# Revit family: KS Polar plus, DS 20, Ø 10- 88,9
name_source: partatom
category: HLS-Bauteile
revit_build: Autodesk Revit 2018 (Build: 20190510_1515(x64)
units: mm (PartAtom-declared; Revit-internal decimal feet)

## family parameters
Arbeitsebenenbasiert = Ja
Beim Laden mit Abzugskörper schneiden = Nein
Bemaßung runder Anschluss = Durchmesser verwenden
Gemeinsam genutzt = Ja
Immer vertikal = Nein
Raumberechnungspunkt = Nein
Teiletyp = Normal

## types (23) — shared parameters
Anschluss = M8/M10
BP = 14 mm  [stored 0.0459318 ft]
Baustoffklasse = B2
DS = 20 mm  [stored 0.0656168 ft]
DVS = 5 mm  [stored 0.0164042 ft]
Dichte Kern = 145 kg/m³
Dämmkörper = AC/PU
Dämmstärke = 20 mm  [stored 0.0656168 ft]
Fabrikat = MEFA
Firma = MEFA Befestigungs- und Montagesysteme GmbH
HGA = 17 mm  [stored 0.0557743 ft]
Kurztext1 = Kälteschelle Polar Plus
Material = Stahl
Materialname = DD11
Mengeneinheit = St
Oberflaeche = galvanisch verzinkt
Rohrschellentyp = Omnia MB
Vorgabe-Ansicht = 1219 mm
Wasserdampfdiffusionswiderstand = 7000 µ
Wärmeleitfähigkeit = 0.031 W/mK
d1 = 7 mm  [stored 0.0229659 ft]
max. Temperaturbeständigkeit = 105 °C
mittl. Nenndruckfestigkeit Kern = 1,9 N/mm²
stat. Belastung Kern = 0,38 N/mm²

## per-type parameters (varying)
- Kälteschelle Polar plus, DS 20, M8/M10, Ø 10: A=39 mm; AB=0 mm  [stored 0 ft]; Anschlußhöhe=37 mm; Artikelnummer=74620100; B=89 mm; Breite=89 mm; D=10 mm  [stored 0.0328084 ft]; D0=50 mm; DF1=16 mm  [stored 0.0524934 ft]; DF2=14 mm  [stored 0.0459318 ft]; Dmax=15 mm  [stored 0.0492126 ft]; Dmin=10 mm  [stored 0.0328084 ft]; EAN=4250928448651; Gewicht=0.11 kg; Gewicht pro Bauteil=0.11 kg; H=71 mm; Kurztext2=10 mm Iso 20 x 36 mm M8/M10; L=36 mm  [stored 0.11811 ft]; MB=20 mm  [stored 0.0656168 ft]; MD=2 mm  [stored 0.00656168 ft]; R=25 mm  [stored 0.082021 ft]; RM=27 mm; Rohraußendurchmesser Kupfer=10 mm; S=73 mm; Schalenlänge=36 mm; max. zul. Last=0.18 kN; vpe=20 St
- Kälteschelle Polar plus, DS 20, M8/M10, Ø 17,2: A=39 mm; AB=1 mm  [stored 0.00328084 ft]; Anschlußhöhe=38 mm; Artikelnummer=74620170; B=92 mm; Breite=92 mm; D=17 mm  [stored 0.0557743 ft]; D0=57 mm; DF1=15 mm  [stored 0.0492126 ft]; DF2=15 mm  [stored 0.0492126 ft]; Dmax=18 mm  [stored 0.0590551 ft]; Dmin=16 mm  [stored 0.0524934 ft]; EAN=4250928442451; Gewicht=0.12 kg; Gewicht pro Bauteil=0.12 kg; H=78 mm; Kurztext2=17,2 mm Iso 20 x 36 mm M8/M10; L=36 mm  [stored 0.11811 ft]; MB=20 mm  [stored 0.0656168 ft]; MD=2 mm  [stored 0.00656168 ft]; R=29 mm; RM=31 mm; Rohraußendurchmesser Stahl=17,2 mm; S=77 mm; Schalenlänge=36 mm; max. zul. Last=0.21 kN; vpe=20 St
- Kälteschelle Polar plus, DS 20, M8/M10, Ø 26,9: A=39 mm; AB=0 mm  [stored 0 ft]; Anschlußhöhe=37 mm; Artikelnummer=74620270; B=101 mm; Breite=101 mm; D=27 mm; D0=67 mm; DF1=14 mm  [stored 0.0459318 ft]; DF2=15 mm  [stored 0.0492126 ft]; Dmax=28 mm; Dmin=27 mm; EAN=4250928442499; Gewicht=0.13 kg; Gewicht pro Bauteil=0.13 kg; H=88 mm; Kurztext2=26,9 mm Iso 20 x 36 mm M8/M10; L=36 mm  [stored 0.11811 ft]; MB=20 mm  [stored 0.0656168 ft]; MD=2 mm  [stored 0.00656168 ft]; R=33 mm; RM=35 mm  [stored 0.114829 ft]; Rohraußendurchmesser Stahl=26,9 mm; S=87 mm; Schalenlänge=36 mm; max. zul. Last=0.32 kN; vpe=20 St
- Kälteschelle Polar plus, DS 20, M8/M10, Ø 32: A=39 mm; AB=0 mm  [stored 0 ft]; Anschlußhöhe=40 mm; Artikelnummer=74620320; B=113 mm; Breite=113 mm; D=32 mm; D0=72 mm; DF1=16 mm  [stored 0.0524934 ft]; DF2=16 mm  [stored 0.0524934 ft]; Dmax=37 mm; Dmin=32 mm; EAN=4250928442512; Gewicht=0.14 kg; Gewicht pro Bauteil=0.14 kg; H=93 mm; Kurztext2=32 mm Iso 20 x 36 mm M8/M10; L=36 mm  [stored 0.11811 ft]; MB=20 mm  [stored 0.0656168 ft]; MD=2 mm  [stored 0.00656168 ft]; R=36 mm  [stored 0.11811 ft]; RM=38 mm  [stored 0.124672 ft]; Rohraußendurchmesser Kunststoff=32 mm; S=97 mm; Schalenlänge=36 mm; max. zul. Last=0.38 kN; vpe=20 St
- Kälteschelle Polar plus, DS 20, M8/M10, Ø 40: A=39 mm; AB=0 mm  [stored 0 ft]; Anschlußhöhe=40 mm; Artikelnummer=74620400; B=117 mm; Breite=117 mm; D=40 mm; D0=80 mm; DF1=15 mm  [stored 0.0492126 ft]; DF2=15 mm  [stored 0.0492126 ft]; Dmax=43 mm; Dmin=40 mm; EAN=4250928442543; Gewicht=0.15 kg; Gewicht pro Bauteil=0.15 kg; H=101 mm; Kurztext2=40 mm Iso 20 x 36 mm M8/M10; L=36 mm  [stored 0.11811 ft]; MB=20 mm  [stored 0.0656168 ft]; MD=2 mm  [stored 0.00656168 ft]; R=40 mm; RM=42 mm; Rohraußendurchmesser Kunststoff=40 mm; S=102 mm; Schalenlänge=36 mm; max. zul. Last=0.48 kN; vpe=20 St
- Kälteschelle Polar plus, DS 20, M8/M10, Ø 48,3: A=39 mm; AB=0 mm  [stored 0 ft]; Anschlußhöhe=39 mm; Artikelnummer=74620480; B=124 mm; Breite=124 mm; D=48 mm; D0=88 mm; DF1=13 mm; DF2=13 mm; Dmax=54 mm; Dmin=48 mm; EAN=4250928442567; Gewicht=0.16 kg; Gewicht pro Bauteil=0.16 kg; H=109 mm; Kurztext2=48,3 mm Iso 20 x 36 mm M8/M10; L=36 mm  [stored 0.11811 ft]; MB=20 mm  [stored 0.0656168 ft]; MD=2 mm  [stored 0.00656168 ft]; R=44 mm; RM=46 mm  [stored 0.150919 ft]; Rohraußendurchmesser Stahl=48,3 mm; S=111 mm; Schalenlänge=36 mm; max. zul. Last=0.58 kN; vpe=20 St
- Kälteschelle Polar plus, DS 20, M8/M10, Ø 57: A=40 mm; AB=0 mm  [stored 0 ft]; Anschlußhöhe=40 mm; Artikelnummer=74620570; B=136 mm; Breite=136 mm; D=57 mm; D0=97 mm; DF1=15 mm  [stored 0.0492126 ft]; DF2=15 mm  [stored 0.0492126 ft]; Dmax=61 mm; Dmin=57 mm; EAN=4250928442598; Gewicht=0.24 kg; Gewicht pro Bauteil=0.24 kg; H=119 mm; Kurztext2=57 mm Iso 20 x 41 mm M8/M10; L=41 mm; MB=25 mm  [stored 0.082021 ft]; MD=3 mm  [stored 0.00984252 ft]; R=49 mm; RM=51 mm; Rohraußendurchmesser Stahl=57 mm; S=121 mm; Schalenlänge=41 mm; max. zul. Last=0.79 kN; vpe=20 St
- Kälteschelle Polar plus, DS 20, M8/M10, Ø 63,5: A=40 mm; AB=2 mm  [stored 0.00656168 ft]; Anschlußhöhe=39 mm; Artikelnummer=74620640; B=143 mm; Breite=143 mm; D=64 mm; D0=104 mm; DF1=16 mm  [stored 0.0524934 ft]; DF2=16 mm  [stored 0.0524934 ft]; Dmax=66 mm; Dmin=62 mm; EAN=4250928442611; Gewicht=0.25 kg; Gewicht pro Bauteil=0.25 kg; H=126 mm; Kurztext2=63,5 mm Iso 20 x 41 mm M8/M10; L=41 mm; MB=25 mm  [stored 0.082021 ft]; MD=3 mm  [stored 0.00984252 ft]; R=52 mm; RM=55 mm; Rohraußendurchmesser Kupfer=64 mm; Rohraußendurchmesser Stahl=63,5 mm; S=127 mm; Schalenlänge=41 mm; max. zul. Last=0.89 kN; vpe=15 St
- Kälteschelle Polar plus, DS 20, M8/M10, Ø 75: A=40 mm; AB=0 mm  [stored 0 ft]; Anschlußhöhe=39 mm; Artikelnummer=74620750; B=158 mm; Breite=152 mm; D=75 mm; D0=115 mm; DF1=17 mm  [stored 0.0557743 ft]; DF2=16 mm  [stored 0.0524934 ft]; Dmax=80 mm; Dmin=75 mm; EAN=4250928442628; Gewicht=0.28 kg; Gewicht pro Bauteil=0.28 kg; H=137 mm; Kurztext2=75 mm Iso 20 x 41 mm M8/M10; L=41 mm; MB=25 mm  [stored 0.082021 ft]; MD=3 mm  [stored 0.00984252 ft]; R=58 mm; RM=60 mm; Rohraußendurchmesser Kunststoff=75 mm; S=141 mm; Schalenlänge=41 mm; max. zul. Last=1.05 kN; vpe=15 St
- Kälteschelle Polar plus, DS 20, M8/M10, Ø 88,9: A=40 mm; AB=1 mm  [stored 0.00328084 ft]; Anschlußhöhe=39 mm; Artikelnummer=74620890; B=165 mm; Breite=165 mm; D=89 mm; D0=129 mm; DF1=15 mm  [stored 0.0492126 ft]; DF2=15 mm  [stored 0.0492126 ft]; Dmax=90 mm; Dmin=88 mm; EAN=4250928442642; Gewicht=0.30 kg; Gewicht pro Bauteil=0.30 kg; H=151 mm; Kurztext2=88,9 mm Iso 20 x 41 mm M8/M10; L=41 mm; MB=25 mm  [stored 0.082021 ft]; MD=3 mm  [stored 0.00984252 ft]; R=64 mm; RM=67 mm; Rohraußendurchmesser Stahl=88,9 mm; S=150 mm; Schalenlänge=41 mm; max. zul. Last=1.24 kN; vpe=15 St
- Kälteschelle Polar plus, DS 20, M8/M10, Ø 12: A=39 mm; AB=2 mm  [stored 0.00656168 ft]; Anschlußhöhe=37 mm; Artikelnummer=74620120; B=89 mm; Breite=89 mm; D=12 mm  [stored 0.0393701 ft]; D0=52 mm; DF1=16 mm  [stored 0.0524934 ft]; DF2=14 mm  [stored 0.0459318 ft]; Dmax=15 mm  [stored 0.0492126 ft]; Dmin=10 mm  [stored 0.0328084 ft]; EAN=4250928448668; Gewicht=0.11 kg; Gewicht pro Bauteil=0.11 kg; H=73 mm; Kurztext2=12 mm Iso 20 x 36 mm M8/M10; L=36 mm  [stored 0.11811 ft]; MB=20 mm  [stored 0.0656168 ft]; MD=2 mm  [stored 0.00656168 ft]; R=26 mm; RM=28 mm; Rohraußendurchmesser Kupfer=12 mm; S=73 mm; Schalenlänge=36 mm; max. zul. Last=0.18 kN; vpe=20 St
- Kälteschelle Polar plus, DS 20, M8/M10, Ø 15: A=39 mm; AB=5 mm  [stored 0.0164042 ft]; Anschlußhöhe=37 mm; Artikelnummer=74620150; B=89 mm; Breite=89 mm; D=15 mm  [stored 0.0492126 ft]; D0=55 mm; DF1=16 mm  [stored 0.0524934 ft]; DF2=14 mm  [stored 0.0459318 ft]; Dmax=15 mm  [stored 0.0492126 ft]; Dmin=10 mm  [stored 0.0328084 ft]; EAN=4250928442444; Gewicht=0.11 kg; Gewicht pro Bauteil=0.11 kg; H=76 mm; Kurztext2=15 mm Iso 20 x 36 mm M8/M10; L=36 mm  [stored 0.11811 ft]; MB=20 mm  [stored 0.0656168 ft]; MD=2 mm  [stored 0.00656168 ft]; R=28 mm; RM=30 mm  [stored 0.0984252 ft]; Rohraußendurchmesser Kupfer=15 mm; S=73 mm; Schalenlänge=36 mm; max. zul. Last=0.18 kN; vpe=20 St
- Kälteschelle Polar plus, DS 20, M8/M10, Ø 18: A=39 mm; AB=2 mm  [stored 0.00656168 ft]; Anschlußhöhe=38 mm; Artikelnummer=74620180; B=92 mm; Breite=92 mm; D=18 mm  [stored 0.0590551 ft]; D0=58 mm; DF1=15 mm  [stored 0.0492126 ft]; DF2=15 mm  [stored 0.0492126 ft]; Dmax=18 mm  [stored 0.0590551 ft]; Dmin=16 mm  [stored 0.0524934 ft]; EAN=4250928442468; Gewicht=0.12 kg; Gewicht pro Bauteil=0.12 kg; H=79 mm; Kurztext2=18 mm Iso 20 x 36 mm M8/M10; L=36 mm  [stored 0.11811 ft]; MB=20 mm  [stored 0.0656168 ft]; MD=2 mm  [stored 0.00656168 ft]; R=29 mm; RM=31 mm; Rohraußendurchmesser Kupfer=18 mm; S=77 mm; Schalenlänge=36 mm; max. zul. Last=0.21 kN; vpe=20 St
- Kälteschelle Polar plus, DS 20, M8/M10, Ø 21,3: A=39 mm; AB=0 mm  [stored 0 ft]; Anschlußhöhe=37 mm; Artikelnummer=74620210; B=92 mm; Breite=92 mm; D=21 mm  [stored 0.0688976 ft]; D0=61 mm; DF1=13 mm; DF2=13 mm; Dmax=22 mm  [stored 0.0721785 ft]; Dmin=21 mm  [stored 0.0688976 ft]; EAN=4250928442475; Gewicht=0.12 kg; Gewicht pro Bauteil=0.12 kg; H=82 mm; Kurztext2=21,3 mm Iso 20 x 36 mm M8/M10; L=36 mm  [stored 0.11811 ft]; MB=20 mm  [stored 0.0656168 ft]; MD=2 mm  [stored 0.00656168 ft]; R=31 mm; RM=33 mm; Rohraußendurchmesser Stahl=21,3 mm; S=79 mm; Schalenlänge=36 mm; max. zul. Last=0.25 kN; vpe=20 St
- Kälteschelle Polar plus, DS 20, M8/M10, Ø 22: A=39 mm; AB=1 mm  [stored 0.00328084 ft]; Anschlußhöhe=37 mm; Artikelnummer=74620220; B=92 mm; Breite=92 mm; D=22 mm  [stored 0.0721785 ft]; D0=62 mm; DF1=13 mm; DF2=13 mm; Dmax=22 mm  [stored 0.0721785 ft]; Dmin=21 mm  [stored 0.0688976 ft]; EAN=4250928442482; Gewicht=0.12 kg; Gewicht pro Bauteil=0.12 kg; H=83 mm; Kurztext2=22 mm Iso 20 x 36 mm M8/M10; L=36 mm  [stored 0.11811 ft]; MB=20 mm  [stored 0.0656168 ft]; MD=2 mm  [stored 0.00656168 ft]; R=31 mm; RM=33 mm; Rohraußendurchmesser Kupfer=22 mm; S=79 mm; Schalenlänge=36 mm; max. zul. Last=0.26 kN; vpe=20 St
- Kälteschelle Polar plus, DS 20, M8/M10, Ø 28: A=39 mm; AB=1 mm  [stored 0.00328084 ft]; Anschlußhöhe=37 mm; Artikelnummer=74620280; B=101 mm; Breite=101 mm; D=28 mm; D0=68 mm; DF1=14 mm  [stored 0.0459318 ft]; DF2=15 mm  [stored 0.0492126 ft]; Dmax=28 mm; Dmin=27 mm; EAN=4250928442505; Gewicht=0.13 kg; Gewicht pro Bauteil=0.13 kg; H=89 mm; Kurztext2=28 mm Iso 20 x 36 mm M8/M10; L=36 mm  [stored 0.11811 ft]; MB=20 mm  [stored 0.0656168 ft]; MD=2 mm  [stored 0.00656168 ft]; R=34 mm; RM=36 mm  [stored 0.11811 ft]; Rohraußendurchmesser Kupfer=28 mm; S=87 mm; Schalenlänge=36 mm; max. zul. Last=0.33 kN; vpe=20 St
- Kälteschelle Polar plus, DS 20, M8/M10, Ø 33,7: A=39 mm; AB=2 mm  [stored 0.00656168 ft]; Anschlußhöhe=38 mm; Artikelnummer=74620340; B=113 mm; Breite=113 mm; D=34 mm; D0=74 mm; DF1=16 mm  [stored 0.0524934 ft]; DF2=16 mm  [stored 0.0524934 ft]; Dmax=37 mm; Dmin=32 mm; EAN=4250928442529; Gewicht=0.14 kg; Gewicht pro Bauteil=0.14 kg; H=95 mm; Kurztext2=33,7 mm Iso 20 x 36 mm M8/M10; L=36 mm  [stored 0.11811 ft]; MB=20 mm  [stored 0.0656168 ft]; MD=2 mm  [stored 0.00656168 ft]; R=37 mm; RM=39 mm; Rohraußendurchmesser Stahl=33,7 mm; S=97 mm; Schalenlänge=36 mm; max. zul. Last=0.40 kN; vpe=20 St
- Kälteschelle Polar plus, DS 20, M8/M10, Ø 35: A=39 mm; AB=3 mm  [stored 0.00984252 ft]; Anschlußhöhe=38 mm; Artikelnummer=74620350; B=113 mm; Breite=113 mm; D=35 mm  [stored 0.114829 ft]; D0=75 mm; DF1=16 mm  [stored 0.0524934 ft]; DF2=16 mm  [stored 0.0524934 ft]; Dmax=37 mm; Dmin=32 mm; EAN=4250928442536; Gewicht=0.14 kg; Gewicht pro Bauteil=0.14 kg; H=96 mm; Kurztext2=35 mm Iso 20 x 36 mm M8/M10; L=36 mm  [stored 0.11811 ft]; MB=20 mm  [stored 0.0656168 ft]; MD=2 mm  [stored 0.00656168 ft]; R=38 mm  [stored 0.124672 ft]; RM=40 mm; Rohraußendurchmesser Kupfer=35 mm; S=97 mm; Schalenlänge=36 mm; max. zul. Last=0.42 kN; vpe=20 St
- Kälteschelle Polar plus, DS 20, M8/M10, Ø 42,4: A=39 mm; AB=2 mm  [stored 0.00656168 ft]; Anschlußhöhe=38 mm; Artikelnummer=74620430; B=117 mm; Breite=117 mm; D=42 mm; D0=82 mm; DF1=15 mm  [stored 0.0492126 ft]; DF2=15 mm  [stored 0.0492126 ft]; Dmax=43 mm; Dmin=40 mm; EAN=4250928442550; Gewicht=0.15 kg; Gewicht pro Bauteil=0.15 kg; H=103 mm; Kurztext2=42,4 mm Iso 20 x 36 mm M8/M10; L=36 mm  [stored 0.11811 ft]; MB=20 mm  [stored 0.0656168 ft]; MD=2 mm  [stored 0.00656168 ft]; R=41 mm; RM=43 mm; Rohraußendurchmesser Kupfer=42 mm; Rohraußendurchmesser Stahl=42,4 mm; S=102 mm; Schalenlänge=36 mm; max. zul. Last=0.51 kN; vpe=20 St
- Kälteschelle Polar plus, DS 20, M8/M10, Ø 50: A=39 mm; AB=2 mm  [stored 0.00656168 ft]; Anschlußhöhe=39 mm; Artikelnummer=74620500; B=124 mm; Breite=124 mm; D=50 mm; D0=90 mm; DF1=13 mm; DF2=13 mm; Dmax=54 mm; Dmin=48 mm; EAN=4250928442574; Gewicht=0.16 kg; Gewicht pro Bauteil=0.16 kg; H=111 mm; Kurztext2=50 mm Iso 20 x 36 mm M8/M10; L=36 mm  [stored 0.11811 ft]; MB=20 mm  [stored 0.0656168 ft]; MD=2 mm  [stored 0.00656168 ft]; R=45 mm; RM=47 mm; Rohraußendurchmesser Kunststoff=50 mm; S=111 mm; Schalenlänge=36 mm; max. zul. Last=0.60 kN; vpe=20 St
- Kälteschelle Polar plus, DS 20, M8/M10, Ø 54: A=39 mm; AB=6 mm  [stored 0.019685 ft]; Anschlußhöhe=37 mm; Artikelnummer=74620540; B=124 mm; Breite=124 mm; D=54 mm; D0=94 mm; DF1=13 mm; DF2=13 mm; Dmax=54 mm; Dmin=48 mm; EAN=4250928442581; Gewicht=0.16 kg; Gewicht pro Bauteil=0.16 kg; H=115 mm; Kurztext2=54 mm Iso 20 x 36 mm M8/M10; L=36 mm  [stored 0.11811 ft]; MB=20 mm  [stored 0.0656168 ft]; MD=2 mm  [stored 0.00656168 ft]; R=47 mm; RM=49 mm; Rohraußendurchmesser Kupfer=54 mm; S=111 mm; Schalenlänge=36 mm; max. zul. Last=0.65 kN; vpe=20 St
- Kälteschelle Polar plus, DS 20, M8/M10, Ø 60,3: A=40 mm; AB=3 mm  [stored 0.00984252 ft]; Anschlußhöhe=38 mm; Artikelnummer=74620600; B=136 mm; Breite=136 mm; D=60 mm; D0=100 mm; DF1=15 mm  [stored 0.0492126 ft]; DF2=15 mm  [stored 0.0492126 ft]; Dmax=61 mm; Dmin=57 mm; EAN=4250928442604; Gewicht=0.24 kg; Gewicht pro Bauteil=0.24 kg; H=122 mm; Kurztext2=60,3 mm Iso 20 x 41 mm M8/M10; L=41 mm; MB=25 mm  [stored 0.082021 ft]; MD=3 mm  [stored 0.00984252 ft]; R=50 mm; RM=53 mm; Rohraußendurchmesser Stahl=60,3 mm; S=121 mm; Schalenlänge=41 mm; max. zul. Last=0.84 kN; vpe=15 St
- Kälteschelle Polar plus, DS 20, M8/M10, Ø 76,1: A=40 mm; AB=1 mm  [stored 0.00328084 ft]; Anschlußhöhe=38 mm; Artikelnummer=74620760; B=158 mm; Breite=152 mm; D=76 mm; D0=116 mm; DF1=17 mm  [stored 0.0557743 ft]; DF2=16 mm  [stored 0.0524934 ft]; Dmax=80 mm; Dmin=75 mm; EAN=4250928442635; Gewicht=0.28 kg; Gewicht pro Bauteil=0.28 kg; H=138 mm; Kurztext2=76,1 mm Iso 20 x 41 mm M8/M10; L=41 mm; MB=25 mm  [stored 0.082021 ft]; MD=3 mm  [stored 0.00984252 ft]; R=58 mm; RM=61 mm; Rohraußendurchmesser Stahl=76,1 mm; S=141 mm; Schalenlänge=41 mm; max. zul. Last=1.06 kN; vpe=15 St

note: [stored X ft] marks values corroborated as IEEE doubles in the binary element streams (Revit-internal decimal feet)

## geometry (parser evidence)
native form markers: Sweep x1
no freeform markers — native parametric forms only
